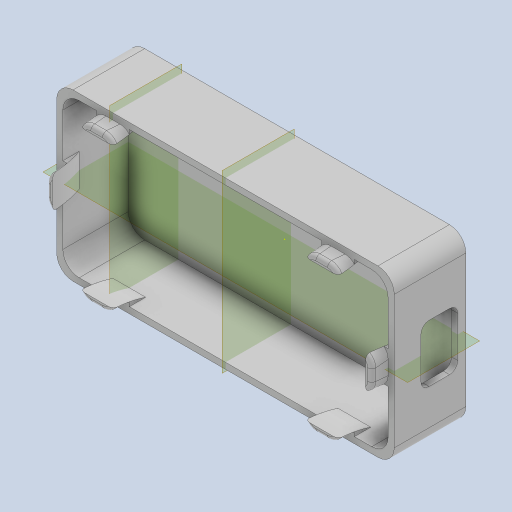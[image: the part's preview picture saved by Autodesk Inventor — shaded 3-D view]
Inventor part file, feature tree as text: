
AUTODESK INVENTOR PART (.ipt)
format: ipt  version: 2024 (Build 280153000, 153)  size: 487,424 bytes
history: native  units: mm
features: fillet x9, sketch x8, extrude x7, other x6, mirror x6, plane x3
ambient origin geometry x8: Origin, YZ Plane, XZ Plane, XY Plane, X Axis, Y Axis, Z Axis, Center Point
bodies: Body1 (feature_tree)
feature tree (39):
  other  "Sólido1"
  extrude  "Extrusión1"  Depth=1.5mm
  extrude  "Extrusión2"  Depth=14.0mm
  extrude  "Extrusión3"  Depth=20.75mm
  fillet  "Empalme1"  Radius=13.75mm
  plane  "Plano de trabajo1"
  plane  "Plano de trabajo2"
  extrude  "Extrusión4"  Depth=2.0mm
  fillet  "Empalme2"  Radius=16.0mm
  mirror  "Simetría1"
  mirror  "Simetría2"
  fillet  "Empalme3"  Radius=2.0mm
  sketch  "Boceto5"  dims[d17=39.75mm d18=18.75mm d24=8.0mm d25=30.0mm]
  extrude  "Extrusión5"  Depth=18.75mm
  fillet  "Empalme4"  Radius=8.0mm
  fillet  "Empalme5"  Radius=30.0mm
  mirror  "Simetría3"
  extrude  "Extrusión6"  Depth=8.0mm TaperAngle=0.0deg
  fillet  "Empalme6"  Radius=2.0mm
  fillet  "Empalme7"  Radius=4.0mm
  mirror  "Simetría4"
  plane  "Plano de trabajo3"
  extrude  "Extrusión7"  Depth=8.0mm
  fillet  "Empalme8"  Radius=30.0mm
  fillet  "Empalme9"  Radius=8.0mm
  mirror  "Simetría5"
  mirror  "Simetría6"
  sketch  "Boceto1"  dims[d4=0.0mm d5=1.5mm]
  sketch  "Boceto2"  dims[d6=16.0mm d7=0.0mm d8=14.0mm]
  sketch  "Boceto3"  dims[d9=9.0mm d10=20.75mm d11=13.75mm]
  sketch  "Boceto4"  dims[d12=12.75mm d13=2.0mm d14=16.0mm d15=0.0mm d16=2.0mm]
  sketch  "Boceto6"  dims[d26=1.5mm d27=8.0mm d28=0.0mm d29=2.0mm d30=4.0mm]
  sketch  "Boceto7"  dims[d31=1.5mm d32=8.0mm d33=30.0mm d34=8.0mm d35=0.0mm]
  sketch  "Boceto8"  dims[d36=3.0mm d37=1.0mm d38=1.5mm d39=8.0mm d40=30.0mm d41=8.0mm d42=0.0mm d43=3.0mm d44=1.0mm d45=27.5mm d46=1.5mm d47=8.0mm d48=30.0mm d49=1.5mm d50=8.0mm d51=0.0mm d52=3.0mm d53=1.0mm]
  other  "Proyectar aristas de corte1"
  other  "Proyectar aristas de corte2"
  other  "Proyectar aristas de corte3"
  other  "Proyectar aristas de corte4"
  other  "Proyectar aristas de corte5"
